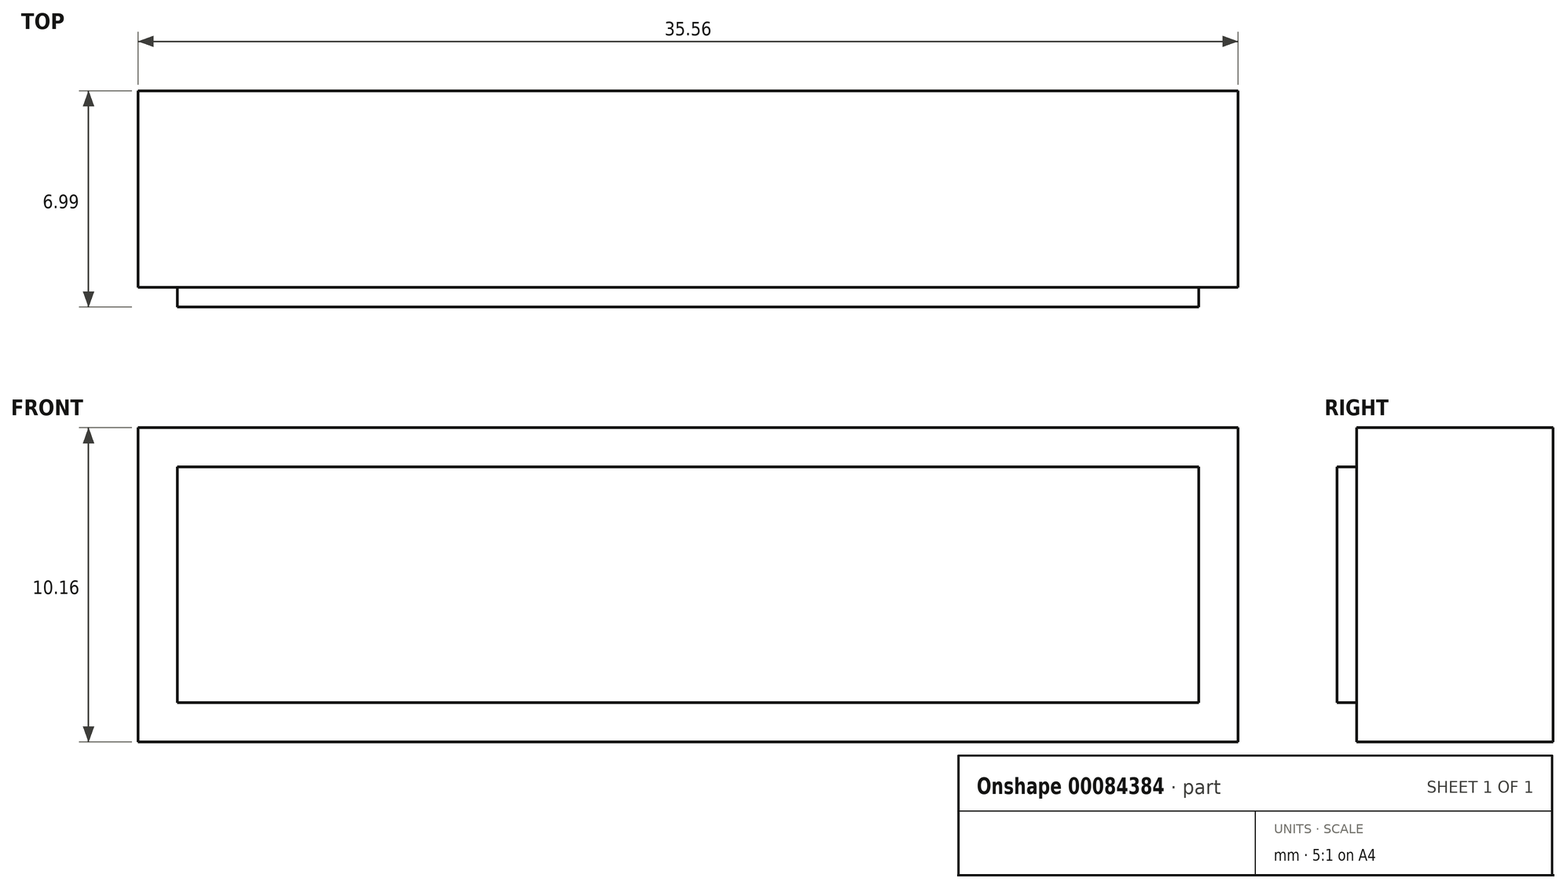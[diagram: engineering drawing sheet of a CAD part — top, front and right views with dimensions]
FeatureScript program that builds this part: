
annotation { "Feature Type Name" : "Feature", "Feature Type Description" : "" }
export const myFeature = defineFeature(function(context is Context, id is Id, definition is map)
    precondition{}
    {
        {
            var Q0;
            Q0=qCreatedBy(makeId("Front.planeOp"),FACE);
            var sketch = newSketch(context, id + "F0", { "sketchPlane" : qUnion([Q0])});
            skLineSegment(sketch, "E0.bottom", {"start": v(-16.05, 2.15) * mm, "end": v(19.51, 2.15) * mm});
            skLineSegment(sketch, "E0.top", {"start": v(-16.05, -8) * mm, "end": v(19.51, -8) * mm});
            skLineSegment(sketch, "E0.left", {"start": v(-16.05, 2.15) * mm, "end": v(-16.05, -8) * mm});
            skLineSegment(sketch, "E0.right", {"start": v(19.51, 2.15) * mm, "end": v(19.51, -8) * mm});
            skSolve(sketch);
        }
        {
            var Q0;
            Q0 = qSketchRegion(id + "F0", true);
            extrude(context, id + "F1", {"entities" : qUnion([Q0]), "depth" : 6.35 * mm});
        }
        {
            var Q0;
            Q0=makeQuery(id+"F1.opExtrude","CAP_FACE",FACE,{"disambiguationData":[OSD([sQuery(id+"F0.wireOp",EDGE,"E0.bottom"),sQuery(id+"F0.wireOp",EDGE,"E0.top"),sQuery(id+"F0.wireOp",EDGE,"E0.left"),sQuery(id+"F0.wireOp",EDGE,"E0.right")])],"isStart":false});
            var sketch = newSketch(context, id + "F2", { "sketchPlane" : qUnion([Q0])});
            skLineSegment(sketch, "E1.bottom", {"start": v(-14.78, 0.88) * mm, "end": v(18.24, 0.88) * mm});
            skLineSegment(sketch, "E1.top", {"start": v(-14.78, -6.74) * mm, "end": v(18.24, -6.74) * mm});
            skLineSegment(sketch, "E1.left", {"start": v(-14.78, 0.88) * mm, "end": v(-14.78, -6.74) * mm});
            skLineSegment(sketch, "E1.right", {"start": v(18.24, 0.88) * mm, "end": v(18.24, -6.74) * mm});
            skSolve(sketch);
        }
        {
            var Q0;
            Q0 = qSketchRegion(id + "F2", true);
            extrude(context, id + "F3", {"entities" : qUnion([Q0]), "operationType" : NewBodyOperationType.ADD, "depth" : 0.64 * mm});
        }
    });
